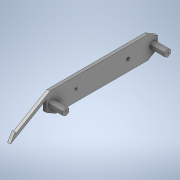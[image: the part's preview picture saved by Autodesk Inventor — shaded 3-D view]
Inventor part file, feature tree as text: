
AUTODESK INVENTOR PART (.ipt)
format: ipt  version: 2020 (Build 240168000, 168)  size: 164,864 bytes
history: native  units: in
note: dims shown in document units (in); Inventor stores cm internally (conversion verified against a paired STEP export)
features: other x3, extrude x1, sketch x1
ambient origin geometry x8: Origin, YZ Plane, XZ Plane, XY Plane, X Axis, Y Axis, Z Axis, Center Point
bodies: Solid1 (feature_tree)
feature tree (5):
  other  "HexWheelGuard.ipt"
  extrude  "Extrusion1"  Depth=0.1575in
  other  "Solid1::HexWheelGuard.ipt"
  other  "TaggingFeature1"
  sketch  "Sketch1"  dims[d0=0.3937in d1=0.0787in d4=60.0deg d5=0.1575in d6=0.0in d7=0.0in d8=1.3898in]
